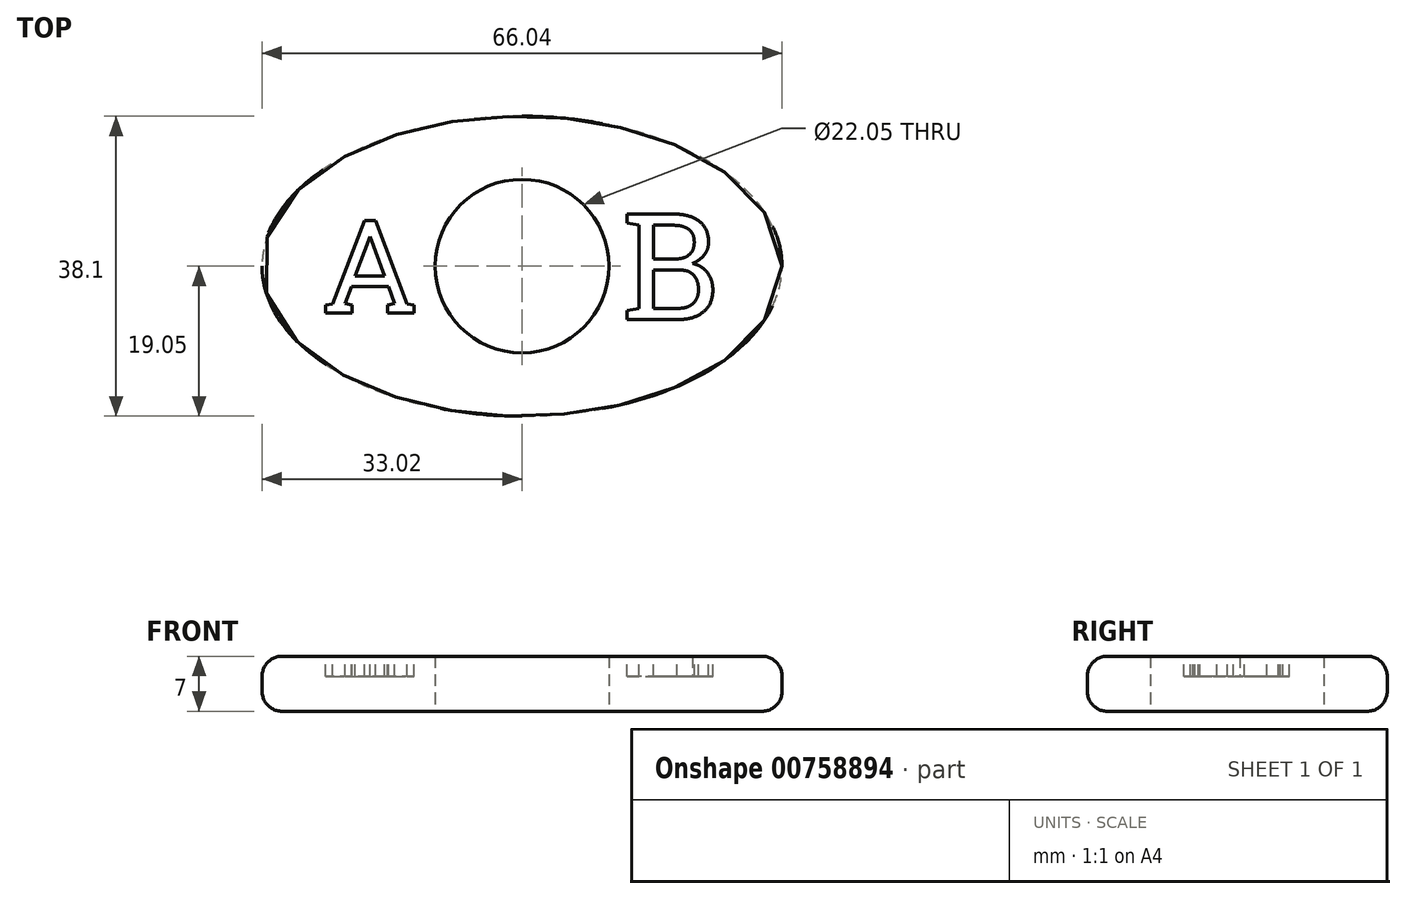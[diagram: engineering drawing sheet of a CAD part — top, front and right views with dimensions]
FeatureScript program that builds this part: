
annotation { "Feature Type Name" : "Feature", "Feature Type Description" : "" }
export const myFeature = defineFeature(function(context is Context, id is Id, definition is map)
    precondition{}
    {
        {
            var Q0;
            Q0=qCreatedBy(makeId("Top.planeOp"),FACE);
            var sketch = newSketch(context, id + "F0", { "sketchPlane" : qUnion([Q0])});
            skEllipse(sketch, "E0", {"center": v(0, 0) * mm, "majorRadius": 33.02 * mm, "minorRadius": 19.05 * mm, "majorAxis": v(1, 0)});
            skCircle(sketch, "E1", {"center": v(0, 0) * mm, "radius": 11.03 * mm});
            skLineSegment(sketch, "E2", {"start": v(-33.02, 0) * mm, "end": v(33.02, 0) * mm, "construction": true});
            skLineSegment(sketch, "E3", {"start": v(0, 19.05) * mm, "end": v(0, -19.05) * mm, "construction": true});
            skSolve(sketch);
        }
        {
            var Q0;
            Q0=makeQuery(id+"F0.imprint","IMPRINT",FACE,{"disambiguationData":[TD([[makeQuery(id+"F0.imprint","IMPRINT",EDGE,{"derivedFrom":sQuery(id+"F0.wireOp",EDGE,"E0")}),1.0]])]});
            extrude(context, id + "F1", {"entities" : qUnion([Q0]), "depth" : 7 * mm, "offsetDistance" : 25.4 * mm});
        }
        {
            var Q0;
            Q0=makeQuery(id+"F1.opExtrude","CAP_EDGE",EDGE,{"disambiguationData":[OSD([sQuery(id+"F0.wireOp",EDGE,"E0")])],"isStart":false});
            var Q1;
            Q1=makeQuery(id+"F1.opExtrude","CAP_EDGE",EDGE,{"disambiguationData":[OSD([sQuery(id+"F0.wireOp",EDGE,"E0")])],"isStart":true});
            fillet(context, id + "F2", {"entities" : qUnion([Q0, Q1]), "radius" : 2.54 * mm, "tangentPropagation" : true, "allowEdgeOverflow" : false});
        }
        {
            var Q0;
            Q0=makeQuery(id+"F1.opExtrude","CAP_FACE",FACE,{"disambiguationData":[OSD([sQuery(id+"F0.wireOp",EDGE,"E0"),sQuery(id+"F0.wireOp",EDGE,"E1")])],"isStart":false});
            var sketch = newSketch(context, id + "F3", { "sketchPlane" : qUnion([Q0])});
            skSolve(sketch);
        }
        {
            var Q0;
            {var subQ0=sQuery(id+"F0.wireOp",EDGE,"E1");Q0=makeQuery(id+"F3.imprint","IMPRINT",FACE,{"disambiguationData":[TD([[makeQuery(id+"F3.imprint","IMPRINT",EDGE,{"derivedFrom":makeQuery(id+"F1.opExtrude","CAP_EDGE",EDGE,{"disambiguationData":[OSD([subQ0])],"isStart":false})}),-1.0]])]});}
            var sketch = newSketch(context, id + "F4", { "sketchPlane" : qUnion([Q0])});
            skText(sketch, "E4", { "text": "A", "fontName": "RobotoSlab-Regular.ttf"});
            skText(sketch, "E5", { "text": "B", "fontName": "RobotoSlab-Regular.ttf"});
            skLineSegment(sketch, "E6", {"start": v(0, 0) * mm, "end": v(-25.4, 0) * mm, "construction": true});
            skLineSegment(sketch, "E7", {"start": v(0, 0) * mm, "end": v(25.4, 0) * mm, "construction": true});
            skLineSegment(sketch, "E8", {"start": v(-25.4, 0) * mm, "end": v(-12.7, 0) * mm, "construction": true});
            skLineSegment(sketch, "E9", {"start": v(12.7, 0) * mm, "end": v(25.4, 0) * mm});
            skPoint(sketch, "E10", {"position": v(19.05, 0) * mm});
            skLineSegment(sketch, "E11", {"start": v(12.7, 0) * mm, "end": v(25.4, 0) * mm, "construction": true});
            skPoint(sketch, "E12", {"position": v(-19.05, 0) * mm});
            const initialGuessF4  = {"E4": [-0.0254, -0.00594, 1, 0, 0.01189], "E5": [0.0127, -0.00678, 1, 0, 0.01357]};
            skSetInitialGuess(sketch, initialGuessF4);
            skSolve(sketch);
        }
        {
            var Q0;
            Q0=qSketchRegion(id+"F4",true);
            extrude(context, id + "F5", {"entities" : qUnion([Q0]), "operationType" : NewBodyOperationType.REMOVE, "oppositeDirection" : true, "depth" : 2.54 * mm, "offsetDistance" : 25.4 * mm});
        }
    });
